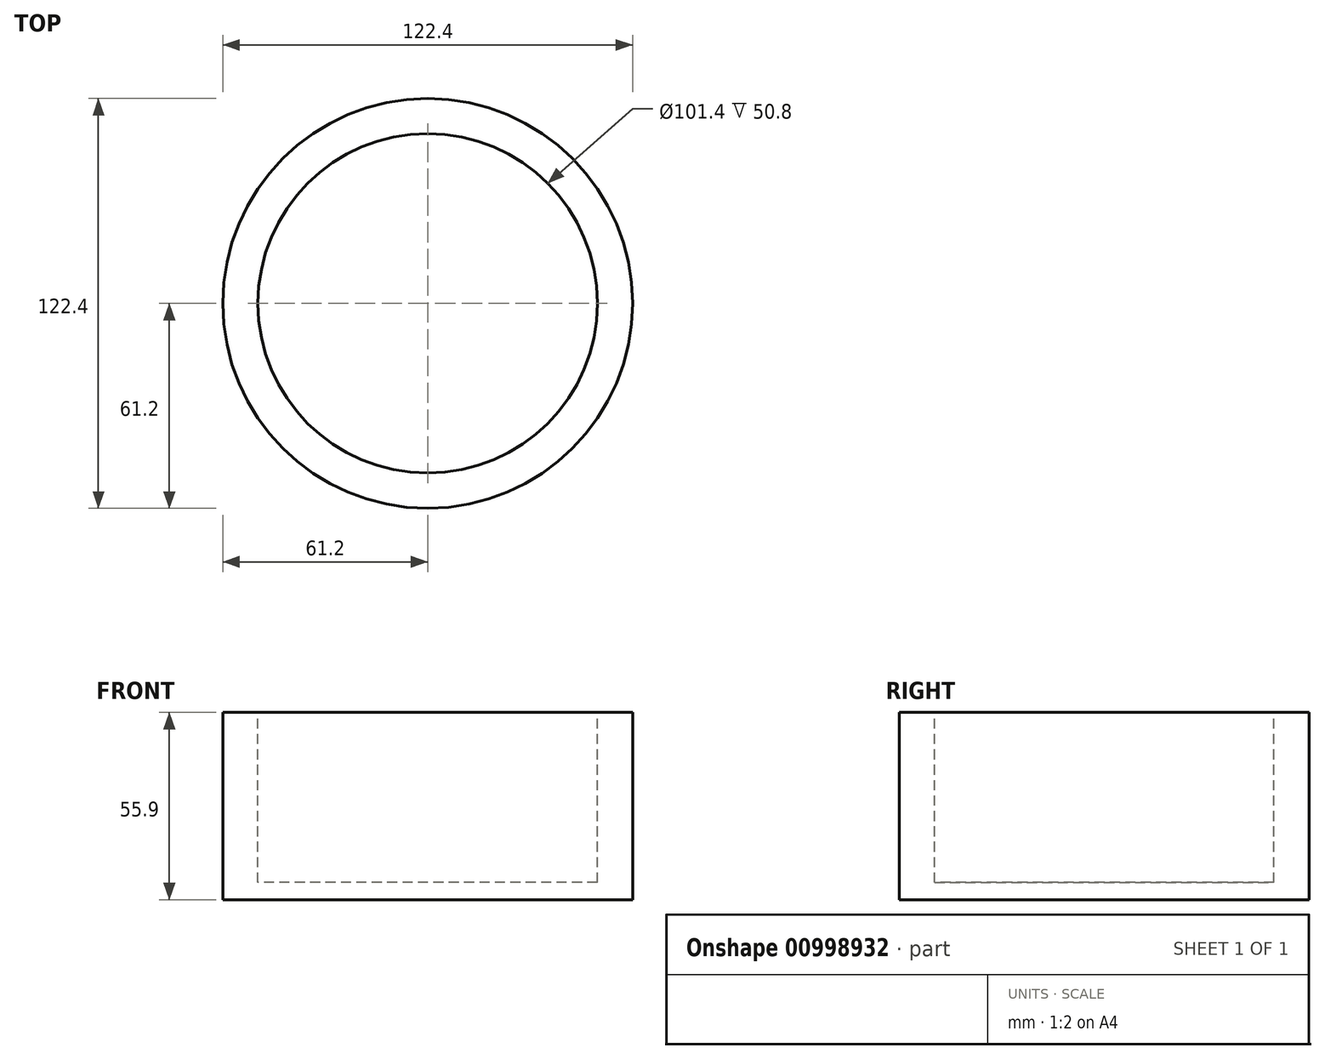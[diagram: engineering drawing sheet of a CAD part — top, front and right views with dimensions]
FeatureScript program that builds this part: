
annotation { "Feature Type Name" : "Feature", "Feature Type Description" : "" }
export const myFeature = defineFeature(function(context is Context, id is Id, definition is map)
    precondition{}
    {
        {
            var Q0;
            Q0=qCreatedBy(makeId("Front.planeOp"),FACE);
            var sketch = newSketch(context, id + "F0", { "sketchPlane" : qUnion([Q0])});
            skLineSegment(sketch, "E0.bottom", {"start": v(0, 0) * mm, "end": v(61.2, 0) * mm});
            skLineSegment(sketch, "E0.top", {"start": v(0, 55.9) * mm, "end": v(61.2, 55.9) * mm});
            skLineSegment(sketch, "E0.left", {"start": v(0, 0) * mm, "end": v(0, 55.9) * mm});
            skLineSegment(sketch, "E0.right", {"start": v(61.2, 0) * mm, "end": v(61.2, 55.9) * mm});
            skLineSegment(sketch, "E1.bottom", {"start": v(0, 0) * mm, "end": v(0, 0) * mm});
            skLineSegment(sketch, "E1.top", {"start": v(0, 111.36) * mm, "end": v(0, 111.36) * mm});
            skLineSegment(sketch, "E1.left", {"start": v(0, 0) * mm, "end": v(0, 111.36) * mm, "construction": true});
            skLineSegment(sketch, "E1.right", {"start": v(0, 0) * mm, "end": v(0, 111.36) * mm, "construction": true});
            skSolve(sketch);
        }
        {
            var Q0;
            Q0=makeQuery(id+"F0.imprint","IMPRINT",FACE,{"disambiguationData":[TD([[makeQuery(id+"F0.imprint","IMPRINT",EDGE,{"derivedFrom":sQuery(id+"F0.wireOp",EDGE,"E0.bottom")}),1.0]])]});
            var Q1;
            Q1=sQuery(id+"F0.wireOp",EDGE,"E1.right");
            revolve(context, id + "F1", {"surfaceOperationType" : NewSurfaceOperationType.NEW, "entities" : qUnion([Q0]), "axis" : qUnion([Q1]), "revolveType" : RevolveType.FULL});
        }
        {
            var Q0;
            Q0=makeQuery(id+"F1.opRevolve","SWEPT_FACE",FACE,{"disambiguationData":[OSD([sQuery(id+"F0.wireOp",EDGE,"E0.top")])]});
            var sketch = newSketch(context, id + "F2", { "sketchPlane" : qUnion([Q0])});
            skCircle(sketch, "E2", {"center": v(0, 0) * mm, "radius": 50.7 * mm});
            skSolve(sketch);
        }
        {
            var Q0;
            Q0 = qSketchRegion(id + "F2", true);
            extrude(context, id + "F3", {"entities" : qUnion([Q0]), "operationType" : NewBodyOperationType.REMOVE, "oppositeDirection" : true, "depth" : 50.8 * mm, "offsetDistance" : 25.4 * mm});
        }
    });
